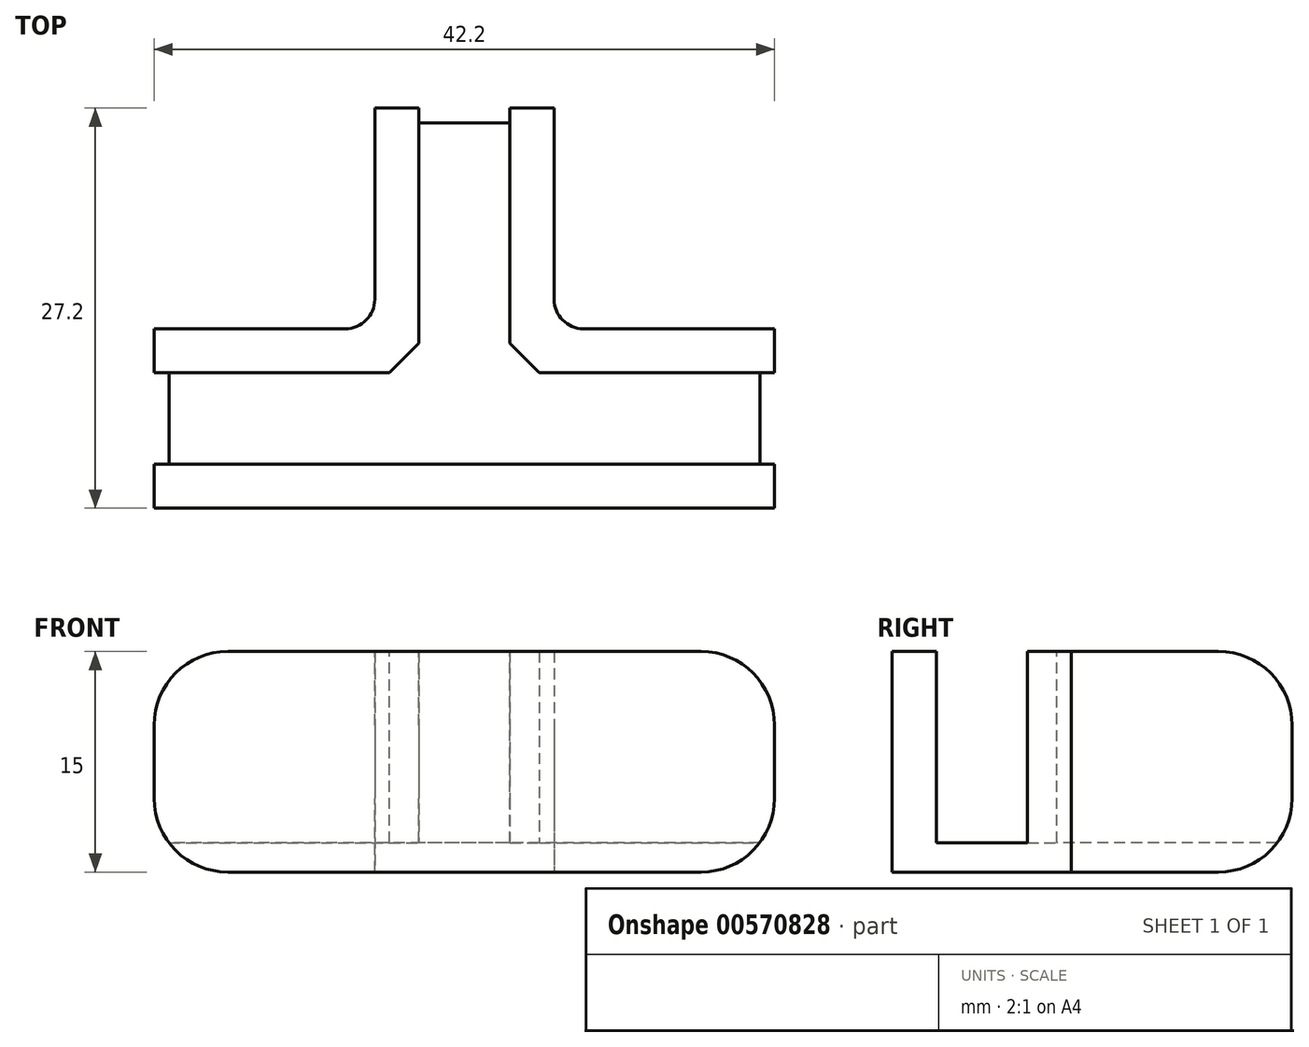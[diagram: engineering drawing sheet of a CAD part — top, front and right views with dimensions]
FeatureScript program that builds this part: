
annotation { "Feature Type Name" : "Feature", "Feature Type Description" : "" }
export const myFeature = defineFeature(function(context is Context, id is Id, definition is map)
    precondition{}
    {
        {
            var Q0;
            Q0=qCreatedBy(makeId("Top.planeOp"),FACE);
            var sketch = newSketch(context, id + "F0", { "sketchPlane" : qUnion([Q0])});
            skLineSegment(sketch, "E0", {"start": v(0, 0) * mm, "end": v(21.1, 0) * mm});
            skLineSegment(sketch, "E1", {"start": v(21.1, 6.2) * mm, "end": v(3.1, 6.2) * mm});
            skLineSegment(sketch, "E2", {"start": v(3.1, 6.2) * mm, "end": v(3.1, 24.2) * mm});
            skLineSegment(sketch, "E3", {"start": v(-3.1, 24.2) * mm, "end": v(-3.1, 6.2) * mm});
            skLineSegment(sketch, "E4", {"start": v(-3.1, 6.2) * mm, "end": v(-21.1, 6.2) * mm});
            skLineSegment(sketch, "E5", {"start": v(-21.1, 0) * mm, "end": v(0, 0) * mm});
            skLineSegment(sketch, "E6.0", {"start": v(6.1, 24.2) * mm, "end": v(-6.1, 24.2) * mm});
            skLineSegment(sketch, "E6.1", {"start": v(6.1, 9.2) * mm, "end": v(6.1, 24.2) * mm});
            skLineSegment(sketch, "E6.2", {"start": v(-6.1, 24.2) * mm, "end": v(-6.1, 9.2) * mm});
            skLineSegment(sketch, "E6.3", {"start": v(21.1, 9.2) * mm, "end": v(6.1, 9.2) * mm});
            skLineSegment(sketch, "E6.4", {"start": v(21.1, -3) * mm, "end": v(21.1, 9.2) * mm});
            skLineSegment(sketch, "E6.5", {"start": v(-6.1, 9.2) * mm, "end": v(-21.1, 9.2) * mm});
            skLineSegment(sketch, "E6.6", {"start": v(-21.1, 9.2) * mm, "end": v(-21.1, -3) * mm});
            skLineSegment(sketch, "E6.7", {"start": v(-21.1, -3) * mm, "end": v(0, -3) * mm});
            skLineSegment(sketch, "E6.8", {"start": v(0, -3) * mm, "end": v(21.1, -3) * mm});
            skPoint(sketch, "E7", {"position": v(0, 24.2) * mm});
            skSolve(sketch);
        }
        {
            var Q0;
            Q0=qSketchRegion(id+"F0",true);
            extrude(context, id + "F1", {"entities" : qUnion([Q0]), "depth" : 2 * mm, "offsetDistance" : 25 * mm});
        }
        {
            var Q0;
            {var subQ4=sQuery(id+"F0.wireOp",EDGE,"E3");Q0=makeQuery(id+"F0.imprint","IMPRINT",FACE,{"disambiguationData":[TD([[makeQuery(id+"F0.imprint","IMPRINT",EDGE,{"derivedFrom":subQ4}),-1.0]])]});}
            var Q1;
            {var subQ3=sQuery(id+"F0.wireOp",EDGE,"E1");Q1=makeQuery(id+"F0.imprint","IMPRINT",FACE,{"disambiguationData":[TD([[makeQuery(id+"F0.imprint","IMPRINT",EDGE,{"derivedFrom":subQ3}),-1.0]])]});}
            var Q2;
            {var subQ4=sQuery(id+"F0.wireOp",EDGE,"E0");Q2=makeQuery(id+"F0.imprint","IMPRINT",FACE,{"disambiguationData":[TD([[makeQuery(id+"F0.imprint","IMPRINT",EDGE,{"derivedFrom":subQ4}),-1.0]])]});}
            extrude(context, id + "F2", {"entities" : qUnion([Q0, Q1, Q2]), "operationType" : NewBodyOperationType.ADD, "depth" : 15 * mm, "offsetDistance" : 25 * mm});
        }
        {
            var Q0;
            {var subQ0=sQuery(id+"F0.wireOp",EDGE,"E6.3");var subQ1=sQuery(id+"F0.wireOp",EDGE,"E6.1");Q0=makeQuery(id+"F2.boolean.opBoolean","MERGE",EDGE,{"derivedFrom":[makeQuery(id+"F1.opExtrude","SWEPT_EDGE",EDGE,{"disambiguationData":[OSD([subQ1,subQ0])]}),makeQuery(id+"F2.opExtrude","SWEPT_EDGE",EDGE,{"disambiguationData":[OSD([subQ1,subQ0])]})]});}
            fillet(context, id + "F3", {"entities" : qUnion([Q0]), "radius" : 2 * mm, "tangentPropagation" : true, "allowEdgeOverflow" : false});
        }
        {
            var Q0;
            {var subQ0=sQuery(id+"F0.wireOp",EDGE,"E6.4");Q0=makeQuery(id+"F2.opExtrude","CAP_EDGE",EDGE,{"disambiguationData":[OSD([subQ0]),TDD([makeQuery(id+"F0.imprint","IMPRINT",EDGE,{"disambiguationData":[TD([[makeQuery(id+"F0.imprint","INTERSECT",VERTEX,{"derivedFrom":[sQuery(id+"F0.wireOp",EDGE,"E0"),subQ0]}),1.0]])],"derivedFrom":subQ0})])],"isStart":false});}
            var Q1;
            {var subQ0=sQuery(id+"F0.wireOp",EDGE,"E6.4");Q1=makeQuery(id+"F2.opExtrude","CAP_EDGE",EDGE,{"disambiguationData":[OSD([subQ0]),TDD([makeQuery(id+"F0.imprint","IMPRINT",EDGE,{"disambiguationData":[TD([[makeQuery(id+"F0.imprint","INTERSECT",VERTEX,{"derivedFrom":[sQuery(id+"F0.wireOp",EDGE,"E1"),subQ0]}),-1.0]])],"derivedFrom":subQ0})])],"isStart":false});}
            var Q2;
            {var subQ0=sQuery(id+"F0.wireOp",EDGE,"E6.6");Q2=makeQuery(id+"F2.opExtrude","CAP_EDGE",EDGE,{"disambiguationData":[OSD([subQ0]),TDD([makeQuery(id+"F0.imprint","IMPRINT",EDGE,{"disambiguationData":[TD([[makeQuery(id+"F0.imprint","INTERSECT",VERTEX,{"derivedFrom":[sQuery(id+"F0.wireOp",EDGE,"E5"),subQ0]}),-1.0]])],"derivedFrom":subQ0})])],"isStart":false});}
            var Q3;
            {var subQ0=sQuery(id+"F0.wireOp",EDGE,"E6.6");Q3=makeQuery(id+"F2.opExtrude","CAP_EDGE",EDGE,{"disambiguationData":[OSD([subQ0]),TDD([makeQuery(id+"F0.imprint","IMPRINT",EDGE,{"disambiguationData":[TD([[makeQuery(id+"F0.imprint","INTERSECT",VERTEX,{"derivedFrom":[sQuery(id+"F0.wireOp",EDGE,"E4"),subQ0]}),1.0]])],"derivedFrom":subQ0})])],"isStart":false});}
            var Q4;
            {var subQ0=sQuery(id+"F0.wireOp",EDGE,"E6.0");Q4=makeQuery(id+"F2.opExtrude","CAP_EDGE",EDGE,{"disambiguationData":[OSD([subQ0]),TDD([makeQuery(id+"F0.imprint","IMPRINT",EDGE,{"disambiguationData":[TD([[makeQuery(id+"F0.imprint","INTERSECT",VERTEX,{"derivedFrom":[sQuery(id+"F0.wireOp",EDGE,"E3"),subQ0]}),-1.0]])],"derivedFrom":subQ0})])],"isStart":false});}
            var Q5;
            {var subQ0=sQuery(id+"F0.wireOp",EDGE,"E6.0");Q5=makeQuery(id+"F2.opExtrude","CAP_EDGE",EDGE,{"disambiguationData":[OSD([subQ0]),TDD([makeQuery(id+"F0.imprint","IMPRINT",EDGE,{"disambiguationData":[TD([[makeQuery(id+"F0.imprint","INTERSECT",VERTEX,{"derivedFrom":[sQuery(id+"F0.wireOp",EDGE,"E2"),subQ0]}),1.0]])],"derivedFrom":subQ0})])],"isStart":false});}
            var Q6;
            Q6=makeQuery(id+"F1.opExtrude","CAP_EDGE",EDGE,{"disambiguationData":[OSD([sQuery(id+"F0.wireOp",EDGE,"E6.6")])],"isStart":true});
            var Q7;
            Q7=makeQuery(id+"F1.opExtrude","CAP_EDGE",EDGE,{"disambiguationData":[OSD([sQuery(id+"F0.wireOp",EDGE,"E6.4")])],"isStart":true});
            var Q8;
            Q8=makeQuery(id+"F1.opExtrude","CAP_EDGE",EDGE,{"disambiguationData":[OSD([sQuery(id+"F0.wireOp",EDGE,"E6.0")])],"isStart":true});
            fillet(context, id + "F4", {"entities" : qUnion([Q0, Q1, Q2, Q3, Q4, Q5, Q6, Q7, Q8]), "radius" : 5 * mm, "tangentPropagation" : true, "allowEdgeOverflow" : false});
        }
        {
            var Q0;
            {var subQ0=sQuery(id+"F0.wireOp",EDGE,"E6.5");var subQ1=sQuery(id+"F0.wireOp",EDGE,"E6.2");Q0=makeQuery(id+"F2.boolean.opBoolean","MERGE",EDGE,{"derivedFrom":[makeQuery(id+"F1.opExtrude","SWEPT_EDGE",EDGE,{"disambiguationData":[OSD([subQ1,subQ0])]}),makeQuery(id+"F2.opExtrude","SWEPT_EDGE",EDGE,{"disambiguationData":[OSD([subQ1,subQ0])]})]});}
            fillet(context, id + "F5", {"entities" : qUnion([Q0]), "radius" : 2 * mm, "tangentPropagation" : true, "allowEdgeOverflow" : false});
        }
        {
            var Q0;
            Q0=makeQuery(id+"F2.opExtrude","SWEPT_EDGE",EDGE,{"disambiguationData":[OSD([sQuery(id+"F0.wireOp",EDGE,"E1"),sQuery(id+"F0.wireOp",EDGE,"E2")])]});
            var Q1;
            Q1=makeQuery(id+"F2.opExtrude","SWEPT_EDGE",EDGE,{"disambiguationData":[OSD([sQuery(id+"F0.wireOp",EDGE,"E3"),sQuery(id+"F0.wireOp",EDGE,"E4")])]});
            chamfer(context, id + "F6", {"entities" : qUnion([Q0, Q1]), "width" : 2 * mm, "tangentPropagation" : true});
        }
    });
